# Revit family: Поли-Групп_ЗатворПоворотныйEAZ-EKT_DN100-2000
name_source: partatom
category: Арматура трубопроводов
units: mm (PartAtom-declared; Revit-internal decimal feet)

## family parameters
Всегда вертикально = Да
На основе рабочей плоскости = Нет
Общий = Нет
При загрузке вырезать с полостями = Нет
Размер круглого соединителя = Использовать диаметр
Тип детали = Клапан - Вставляется

## types (38) — shared parameters
ADSK_URL страницы изделия = https://www.polycorr.ru
ADSK_Версия Revit = 2019
ADSK_Единица измерения = шт.
ADSK_Завод-изготовитель = ООО ПК «Поли-Групп»
ADSK_Количество = 1
ADSK_Материал = Высокопрочный чугун GGG-40
ADSK_Материал наименование = Высокопрочный чугун с шаровидным графитом (GGG-40)
r = 10 мм
Изображение типоразмера = <Нет>
Класс герметичности = ГОСТ Р 9544-2015
Материал Диска = Высокопрочный чугун с шаровидным графитом (GGG-40)
Материал уплотнения = EPDM
Материал штурвала = Сталь окрашенная черная
Назначение = Для установки в качестве запорного устройства на трубопроводах
Покрытия = Высококачественное эпоксидное покрытие толщиной 300 мкм
Рабочая среда = Питьевая вода, техническая вода, морская вода
Разработчик = https://3dbim.pro
Срок службы = 50 лет
ТВ = ЗатворПоворотныйEAZ-EKT_DN100-2000_Поли-Групп
Температура рабочей среды = 0 до +70°С
Тип привода = Редуктор
Тип присоединения = Фланцевое

## per-type parameters (varying)
- 100-10: ADSK_Марка=EAZ-BV-1 DN100 PN10; ADSK_Масса=25; ADSK_Масса_Текст=25; ADSK_Наименование=Затвор поворотный EAZ EKT для воды с мягким уплотнением с двойным эксцентриком. фланцевый DN100 PN10; ADSK_Наименование краткое=Затвор поворотный EAZ EKT DN100 PN10; D=220 мм; D2=156 мм; D3=140 мм; D4=110 мм; DN=100 мм; H1=128 мм; H2=165 мм; Kv=1.0 м³/ч; L=190 мм; PN=10.0 бары; W=250 мм; b=19 мм; d1=113 мм; f=3 мм; h1=45 мм; h2=45 мм; l=125 мм; Вал_d=100 мм; Габаритные размеры=190х220х418; Диск_t=5 мм; Крутящий момент=0; Уши_h=220 мм; Уши_h2=156 мм; Фланец_t=41 мм
- 150-10: ADSK_Марка=EAZ-BV-1 DN150 PN10; ADSK_Масса=40; ADSK_Масса_Текст=40; ADSK_Наименование=Затвор поворотный EAZ EKT для воды с мягким уплотнением с двойным эксцентриком. фланцевый DN150 PN10; ADSK_Наименование краткое=Затвор поворотный EAZ EKT DN150 PN10; D=285 мм; D2=211 мм; D3=190 мм; D4=160 мм; DN=150 мм; H1=166 мм; H2=245 мм; Kv=0.6 м³/ч; L=210 мм; PN=10.0 бары; W=250 мм; b=19 мм; d1=113 мм; f=3 мм; h1=45 мм; h2=45 мм; l=125 мм; Вал_d=100 мм; Габаритные размеры=210х285х536; Диск_t=8 мм; Крутящий момент=0; Уши_h=285 мм; Уши_h2=211 мм; Фланец_t=61 мм
- 200-10: ADSK_Марка=EAZ-BV-1 DN200 PN10; ADSK_Масса=52; ADSK_Масса_Текст=52; ADSK_Наименование=Затвор поворотный EAZ EKT для воды с мягким уплотнением с двойным эксцентриком. фланцевый DN200 PN10; ADSK_Наименование краткое=Затвор поворотный EAZ EKT DN200 PN10; D=340 мм; D2=266 мм; D3=240 мм; D4=210 мм; DN=200 мм; H1=196 мм; H2=270 мм; Kv=0.6 м³/ч; L=230 мм; PN=10.0 бары; W=250 мм; b=20 мм; d1=135 мм; f=3 мм; h1=55 мм; h2=45 мм; l=150 мм; Вал_d=120 мм; Габаритные размеры=230х340х591; Диск_t=10 мм; Крутящий момент=60; Уши_h=340 мм; Уши_h2=266 мм; Фланец_t=68 мм
- 250-10: ADSK_Марка=EAZ-BV-1 DN250 PN10; ADSK_Масса=75; ADSK_Масса_Текст=75; ADSK_Наименование=Затвор поворотный EAZ EKT для воды с мягким уплотнением с двойным эксцентриком. фланцевый DN250 PN10; ADSK_Наименование краткое=Затвор поворотный EAZ EKT DN250 PN10; D=395 мм; D2=319 мм; D3=290 мм; D4=260 мм; DN=250 мм; H1=216 мм; H2=305 мм; Kv=0.5 м³/ч; L=250 мм; PN=10.0 бары; W=280 мм; b=22 мм; d1=135 мм; f=3 мм; h1=55 мм; h2=45 мм; l=150 мм; Вал_d=120 мм; Габаритные размеры=250х395х661; Диск_t=13 мм; Крутящий момент=110; Уши_h=395 мм; Уши_h2=319 мм; Фланец_t=76 мм
- 300-10: ADSK_Марка=EAZ-BV-1 DN300 PN10; ADSK_Масса=110; ADSK_Масса_Текст=110; ADSK_Наименование=Затвор поворотный EAZ EKT для воды с мягким уплотнением с двойным эксцентриком. фланцевый DN300 PN10; ADSK_Наименование краткое=Затвор поворотный EAZ EKT DN300 PN10; D=445 мм; D2=370 мм; D3=340 мм; D4=310 мм; DN=300 мм; H1=245 мм; H2=350 мм; Kv=0.4 м³/ч; L=270 мм; PN=10.0 бары; W=320 мм; b=25 мм; d1=158 мм; f=4 мм; h1=70 мм; h2=45 мм; l=175 мм; Вал_d=140 мм; Габаритные размеры=270х445х755; Диск_t=15 мм; Крутящий момент=150; Уши_h=445 мм; Уши_h2=370 мм; Фланец_t=88 мм
- 350-10: ADSK_Марка=EAZ-BV-1 DN350 PN10; ADSK_Масса=140; ADSK_Масса_Текст=140; ADSK_Наименование=Затвор поворотный EAZ EKT для воды с мягким уплотнением с двойным эксцентриком. фланцевый DN350 PN10; ADSK_Наименование краткое=Затвор поворотный EAZ EKT DN350 PN10; D=505 мм; D2=429 мм; D3=390 мм; D4=360 мм; DN=350 мм; H1=285 мм; H2=395 мм; Kv=0.4 м³/ч; L=290 мм; PN=10.0 бары; W=320 мм; b=25 мм; d1=158 мм; f=4 мм; h1=70 мм; h2=45 мм; l=175 мм; Вал_d=140 мм; Габаритные размеры=290х505х840; Диск_t=18 мм; Крутящий момент=240; Уши_h=505 мм; Уши_h2=429 мм; Фланец_t=99 мм
- 400-10: ADSK_Марка=EAZ-BV-1 DN400 PN10; ADSK_Масса=182; ADSK_Масса_Текст=182; ADSK_Наименование=Затвор поворотный EAZ EKT для воды с мягким уплотнением с двойным эксцентриком. фланцевый DN400 PN10; ADSK_Наименование краткое=Затвор поворотный EAZ EKT DN400 PN10; D=565 мм; D2=480 мм; D3=440 мм; D4=410 мм; DN=400 мм; H1=315 мм; H2=485 мм; Kv=0.3 м³/ч; L=310 мм; PN=10.0 бары; W=350 мм; b=25 мм; d1=189 мм; f=4 мм; h1=85 мм; h2=45 мм; l=210 мм; Вал_d=168 мм; Габаритные размеры=310х565х975; Диск_t=20 мм; Крутящий момент=300; Уши_h=565 мм; Уши_h2=480 мм; Фланец_t=121 мм
- 450-10: ADSK_Марка=EAZ-BV-1 DN450 PN10; ADSK_Масса=230; ADSK_Масса_Текст=230; ADSK_Наименование=Затвор поворотный EAZ EKT для воды с мягким уплотнением с двойным эксцентриком. фланцевый DN450 PN10; ADSK_Наименование краткое=Затвор поворотный EAZ EKT DN450 PN10; D=615 мм; D2=530 мм; D3=490 мм; D4=460 мм; DN=450 мм; H1=335 мм; H2=500 мм; Kv=0.5 м³/ч; L=330 мм; PN=10.0 бары; W=350 мм; b=26 мм; d1=189 мм; f=4 мм; h1=85 мм; h2=58 мм; l=210 мм; Вал_d=168 мм; Габаритные размеры=330х615х1010; Диск_t=23 мм; Крутящий момент=360; Уши_h=615 мм; Уши_h2=530 мм; Фланец_t=125 мм
- 500-10: ADSK_Марка=EAZ-BV-1 DN500 PN10; ADSK_Масса=265; ADSK_Масса_Текст=265; ADSK_Наименование=Затвор поворотный EAZ EKT для воды с мягким уплотнением с двойным эксцентриком. фланцевый DN500 PN10; ADSK_Наименование краткое=Затвор поворотный EAZ EKT DN500 PN10; D=670 мм; D2=582 мм; D3=540 мм; D4=510 мм; DN=500 мм; H1=360 мм; H2=545 мм; Kv=0.4 м³/ч; L=350 мм; PN=10.0 бары; W=400 мм; b=27 мм; d1=234 мм; f=4 мм; h1=85 мм; h2=58 мм; l=260 мм; Вал_d=208 мм; Габаритные размеры=350х670х1105; Диск_t=25 мм; Крутящий момент=430; Уши_h=670 мм; Уши_h2=582 мм; Фланец_t=136 мм
- 600-10: ADSK_Марка=EAZ-BV-1 DN600 PN10; ADSK_Масса=396; ADSK_Масса_Текст=396; ADSK_Наименование=Затвор поворотный EAZ EKT для воды с мягким уплотнением с двойным эксцентриком. фланцевый DN600 PN10; ADSK_Наименование краткое=Затвор поворотный EAZ EKT DN600 PN10; D=780 мм; D2=682 мм; D3=640 мм; D4=610 мм; DN=600 мм; H1=425 мм; H2=595 мм; Kv=0.4 м³/ч; L=390 мм; PN=10.0 бары; W=450 мм; b=30 мм; d1=270 мм; f=5 мм; h1=85 мм; h2=58 мм; l=300 мм; Вал_d=240 мм; Габаритные размеры=390х780х1245; Диск_t=30 мм; Крутящий момент=540; Уши_h=780 мм; Уши_h2=682 мм; Фланец_t=149 мм
- 700-10: ADSK_Марка=EAZ-BV-1 DN700 PN10; ADSK_Масса=550; ADSK_Масса_Текст=550; ADSK_Наименование=Затвор поворотный EAZ EKT для воды с мягким уплотнением с двойным эксцентриком. фланцевый DN700 PN10; ADSK_Наименование краткое=Затвор поворотный EAZ EKT DN700 PN10; D=895 мм; D2=794 мм; D3=740 мм; D4=710 мм; DN=700 мм; H1=490 мм; H2=670 мм; Kv=0.4 м³/ч; L=430 мм; PN=10.0 бары; W=450 мм; b=33 мм; d1=270 мм; f=5 мм; h1=85 мм; h2=60 мм; l=300 мм; Вал_d=240 мм; Габаритные размеры=430х895х1385; Диск_t=35 мм; Крутящий момент=690; Уши_h=895 мм; Уши_h2=794 мм; Фланец_t=168 мм
- 800-10: ADSK_Марка=EAZ-BV-1 DN800 PN10; ADSK_Масса=760; ADSK_Масса_Текст=760; ADSK_Наименование=Затвор поворотный EAZ EKT для воды с мягким уплотнением с двойным эксцентриком. фланцевый DN800 PN10; ADSK_Наименование краткое=Затвор поворотный EAZ EKT DN800 PN10; D=1015 мм; D2=901 мм; D3=840 мм; D4=810 мм; DN=800 мм; H1=552 мм; H2=750 мм; Kv=0.3 м³/ч; L=470 мм; PN=10.0 бары; W=500 мм; b=35 мм; d1=270 мм; f=5 мм; h1=85 мм; h2=60 мм; l=300 мм; Вал_d=240 мм; Габаритные размеры=470х1015х1552; Диск_t=40 мм; Крутящий момент=290; Уши_h=1015 мм; Уши_h2=901 мм; Фланец_t=188 мм
- 900-10: ADSK_Марка=EAZ-BV-1 DN900 PN10; ADSK_Масса=870; ADSK_Масса_Текст=870; ADSK_Наименование=Затвор поворотный EAZ EKT для воды с мягким уплотнением с двойным эксцентриком. фланцевый DN900 PN10; ADSK_Наименование краткое=Затвор поворотный EAZ EKT DN900 PN10; D=1115 мм; D2=1001 мм; D3=940 мм; D4=910 мм; DN=900 мм; H1=600 мм; H2=810 мм; Kv=0.3 м³/ч; L=510 мм; PN=10.0 бары; W=500 мм; b=38 мм; d1=315 мм; f=5 мм; h1=100 мм; h2=60 мм; l=350 мм; Вал_d=280 мм; Габаритные размеры=510х1115х1660; Диск_t=45 мм; Крутящий момент=400; Уши_h=1115 мм; Уши_h2=1001 мм; Фланец_t=203 мм
- 1000-10: ADSK_Марка=EAZ-BV-1 DN1000 PN10; ADSK_Масса=1015; ADSK_Масса_Текст=1015; ADSK_Наименование=Затвор поворотный EAZ EKT для воды с мягким уплотнением с двойным эксцентриком. фланцевый DN1000 PN10; ADSK_Наименование краткое=Затвор поворотный EAZ EKT DN1000 PN10; D=1230 мм; D2=1112 мм; D3=1040 мм; D4=1010 мм; DN=1000 мм; H1=665 мм; H2=885 мм; Kv=0.3 м³/ч; L=550 мм; PN=10.0 бары; W=500 мм; b=40 мм; d1=396 мм; f=5 мм; h1=100 мм; h2=60 мм; l=440 мм; Вал_d=352 мм; Габаритные размеры=550х1230х1800; Диск_t=50 мм; Крутящий момент=310; Уши_h=1230 мм; Уши_h2=1112 мм; Фланец_t=221 мм
- 1200-10: ADSK_Марка=EAZ-BV-1 DN1200 PN10; ADSK_Масса=1885; ADSK_Масса_Текст=1885; ADSK_Наименование=Затвор поворотный EAZ EKT для воды с мягким уплотнением с двойным эксцентриком. фланцевый DN1200 PN10; ADSK_Наименование краткое=Затвор поворотный EAZ EKT DN1200 PN10; D=1455 мм; D2=1328 мм; D3=1240 мм; D4=1210 мм; DN=1200 мм; H1=790 мм; H2=1000 мм; Kv=0.6 м³/ч; L=630 мм; PN=10.0 бары; W=600 мм; b=45 мм; d1=396 мм; f=5 мм; h1=100 мм; h2=70 мм; l=440 мм; Вал_d=352 мм; Габаритные размеры=630х1455х2090; Диск_t=60 мм; Крутящий момент=400; Уши_h=1455 мм; Уши_h2=1328 мм; Фланец_t=250 мм
- 1400-10: ADSK_Марка=EAZ-BV-1 DN1400 PN10; ADSK_Масса=3050; ADSK_Масса_Текст=3050; ADSK_Наименование=Затвор поворотный EAZ EKT для воды с мягким уплотнением с двойным эксцентриком. фланцевый DN1400 PN10; ADSK_Наименование краткое=Затвор поворотный EAZ EKT DN1400 PN10; D=1675 мм; D2=1530 мм; D3=1440 мм; D4=1410 мм; DN=1400 мм; H1=916 мм; H2=1180 мм; Kv=0.2 м³/ч; L=710 мм; PN=10.0 бары; W=650 мм; b=46 мм; d1=432 мм; f=5 мм; h1=125 мм; h2=70 мм; l=480 мм; Вал_d=384 мм; Габаритные размеры=710х1675х2421; Диск_t=70 мм; Крутящий момент=390; Уши_h=1675 мм; Уши_h2=1530 мм; Фланец_t=295 мм
- 1600-10: ADSK_Марка=EAZ-BV-1 DN1600 PN10; ADSK_Масса=4080; ADSK_Масса_Текст=4080; ADSK_Наименование=Затвор поворотный EAZ EKT для воды с мягким уплотнением с двойным эксцентриком. фланцевый DN1600 PN10; ADSK_Наименование краткое=Затвор поворотный EAZ EKT DN1600 PN10; D=1915 мм; D2=1750 мм; D3=1640 мм; D4=1610 мм; DN=1600 мм; H1=1045 мм; H2=1350 мм; Kv=0.2 м³/ч; L=790 мм; PN=10.0 бары; W=700 мм; b=49 мм; d1=432 мм; f=5 мм; h1=125 мм; h2=80 мм; l=480 мм; Вал_d=384 мм; Габаритные размеры=790х1915х2745; Диск_t=80 мм; Крутящий момент=360; Уши_h=1915 мм; Уши_h2=1750 мм; Фланец_t=338 мм
- 1800-10: ADSK_Марка=EAZ-BV-1 DN1800 PN10; ADSK_Масса=5895; ADSK_Масса_Текст=5895; ADSK_Наименование=Затвор поворотный EAZ EKT для воды с мягким уплотнением с двойным эксцентриком. фланцевый DN1800 PN10; ADSK_Наименование краткое=Затвор поворотный EAZ EKT DN1800 PN10; D=2115 мм; D2=1950 мм; D3=1840 мм; D4=1810 мм; DN=1800 мм; H1=1160 мм; H2=1450 мм; Kv=1.0 м³/ч; L=870 мм; PN=10.0 бары; W=750 мм; b=52 мм; d1=468 мм; f=5 мм; h1=125 мм; h2=80 мм; l=520 мм; Вал_d=416 мм; Габаритные размеры=870х2115х2985; Диск_t=90 мм; Крутящий момент=0; Уши_h=2115 мм; Уши_h2=1950 мм; Фланец_t=363 мм
- 2000-10: ADSK_Марка=EAZ-BV-1 DN2000 PN10; ADSK_Масса=7000; ADSK_Масса_Текст=7000; ADSK_Наименование=Затвор поворотный EAZ EKT для воды с мягким уплотнением с двойным эксцентриком. фланцевый DN2000 PN10; ADSK_Наименование краткое=Затвор поворотный EAZ EKT DN2000 PN10; D=2325 мм; D2=2150 мм; D3=2040 мм; D4=2010 мм; DN=2000 мм; H1=1315 мм; H2=1680 мм; Kv=1.0 м³/ч; L=950 мм; PN=10.0 бары; W=800 мм; b=55 мм; d1=468 мм; f=5 мм; h1=150 мм; h2=100 мм; l=520 мм; Вал_d=416 мм; Габаритные размеры=950х2325х3395; Диск_t=100 мм; Крутящий момент=0; Уши_h=2325 мм; Уши_h2=2150 мм; Фланец_t=420 мм
- 100-16: ADSK_Марка=EAZ-BV-1 DN100 PN16; ADSK_Масса=25; ADSK_Масса_Текст=25; ADSK_Наименование=Затвор поворотный EAZ EKT для воды с мягким уплотнением с двойным эксцентриком. фланцевый DN100 PN16; ADSK_Наименование краткое=Затвор поворотный EAZ EKT DN100 PN16; D=220 мм; D2=156 мм; D3=140 мм; D4=110 мм; DN=100 мм; H1=128 мм; H2=165 мм; Kv=1.0 м³/ч; L=190 мм; PN=16.0 бары; W=250 мм; b=19 мм; d1=113 мм; f=3 мм; h1=45 мм; h2=45 мм; l=125 мм; Вал_d=100 мм; Габаритные размеры=190х220х418; Диск_t=5 мм; Крутящий момент=0; Уши_h=220 мм; Уши_h2=156 мм; Фланец_t=41 мм
- 150-16: ADSK_Марка=EAZ-BV-1 DN150 PN16; ADSK_Масса=40; ADSK_Масса_Текст=40; ADSK_Наименование=Затвор поворотный EAZ EKT для воды с мягким уплотнением с двойным эксцентриком. фланцевый DN150 PN16; ADSK_Наименование краткое=Затвор поворотный EAZ EKT DN150 PN16; D=285 мм; D2=211 мм; D3=190 мм; D4=160 мм; DN=150 мм; H1=166 мм; H2=245 мм; Kv=0.6 м³/ч; L=210 мм; PN=16.0 бары; W=250 мм; b=19 мм; d1=113 мм; f=3 мм; h1=45 мм; h2=45 мм; l=125 мм; Вал_d=100 мм; Габаритные размеры=210х285х536; Диск_t=8 мм; Крутящий момент=0; Уши_h=285 мм; Уши_h2=211 мм; Фланец_t=61 мм
- 200-16: ADSK_Марка=EAZ-BV-1 DN200 PN16; ADSK_Масса=56; ADSK_Масса_Текст=56; ADSK_Наименование=Затвор поворотный EAZ EKT для воды с мягким уплотнением с двойным эксцентриком. фланцевый DN200 PN16; ADSK_Наименование краткое=Затвор поворотный EAZ EKT DN200 PN16; D=340 мм; D2=266 мм; D3=240 мм; D4=210 мм; DN=200 мм; H1=196 мм; H2=270 мм; Kv=0.6 м³/ч; L=230 мм; PN=16.0 бары; W=250 мм; b=20 мм; d1=135 мм; f=3 мм; h1=55 мм; h2=45 мм; l=150 мм; Вал_d=120 мм; Габаритные размеры=230х340х591; Диск_t=10 мм; Крутящий момент=90; Уши_h=340 мм; Уши_h2=266 мм; Фланец_t=68 мм
- 250-16: ADSK_Марка=EAZ-BV-1 DN250 PN16; ADSK_Масса=85; ADSK_Масса_Текст=85; ADSK_Наименование=Затвор поворотный EAZ EKT для воды с мягким уплотнением с двойным эксцентриком. фланцевый DN250 PN16; ADSK_Наименование краткое=Затвор поворотный EAZ EKT DN250 PN16; D=405 мм; D2=319 мм; D3=290 мм; D4=260 мм; DN=250 мм; H1=216 мм; H2=305 мм; Kv=0.5 м³/ч; L=250 мм; PN=16.0 бары; W=280 мм; b=22 мм; d1=135 мм; f=3 мм; h1=55 мм; h2=45 мм; l=150 мм; Вал_d=120 мм; Габаритные размеры=250х405х661; Диск_t=13 мм; Крутящий момент=150; Уши_h=405 мм; Уши_h2=319 мм; Фланец_t=76 мм
- 300-16: ADSK_Марка=EAZ-BV-1 DN300 PN16; ADSK_Масса=115; ADSK_Масса_Текст=115; ADSK_Наименование=Затвор поворотный EAZ EKT для воды с мягким уплотнением с двойным эксцентриком. фланцевый DN300 PN16; ADSK_Наименование краткое=Затвор поворотный EAZ EKT DN300 PN16; D=460 мм; D2=370 мм; D3=340 мм; D4=310 мм; DN=300 мм; H1=245 мм; H2=350 мм; Kv=0.4 м³/ч; L=270 мм; PN=16.0 бары; W=320 мм; b=25 мм; d1=158 мм; f=4 мм; h1=70 мм; h2=45 мм; l=175 мм; Вал_d=140 мм; Габаритные размеры=270х460х755; Диск_t=15 мм; Крутящий момент=240; Уши_h=460 мм; Уши_h2=370 мм; Фланец_t=88 мм
- 350-16: ADSK_Марка=EAZ-BV-1 DN350 PN16; ADSK_Масса=150; ADSK_Масса_Текст=150; ADSK_Наименование=Затвор поворотный EAZ EKT для воды с мягким уплотнением с двойным эксцентриком. фланцевый DN350 PN16; ADSK_Наименование краткое=Затвор поворотный EAZ EKT DN350 PN16; D=520 мм; D2=429 мм; D3=390 мм; D4=360 мм; DN=350 мм; H1=285 мм; H2=395 мм; Kv=0.4 м³/ч; L=290 мм; PN=16.0 бары; W=320 мм; b=27 мм; d1=158 мм; f=4 мм; h1=70 мм; h2=45 мм; l=175 мм; Вал_d=140 мм; Габаритные размеры=290х520х840; Диск_t=18 мм; Крутящий момент=300; Уши_h=520 мм; Уши_h2=429 мм; Фланец_t=99 мм
- 400-16: ADSK_Марка=EAZ-BV-1 DN400 PN16; ADSK_Масса=205; ADSK_Масса_Текст=205; ADSK_Наименование=Затвор поворотный EAZ EKT для воды с мягким уплотнением с двойным эксцентриком. фланцевый DN400 PN16; ADSK_Наименование краткое=Затвор поворотный EAZ EKT DN400 PN16; D=580 мм; D2=480 мм; D3=440 мм; D4=410 мм; DN=400 мм; H1=315 мм; H2=485 мм; Kv=0.5 м³/ч; L=310 мм; PN=16.0 бары; W=350 мм; b=28 мм; d1=189 мм; f=4 мм; h1=85 мм; h2=45 мм; l=210 мм; Вал_d=168 мм; Габаритные размеры=310х580х975; Диск_t=20 мм; Крутящий момент=370; Уши_h=580 мм; Уши_h2=480 мм; Фланец_t=121 мм
- 450-16: ADSK_Марка=EAZ-BV-1 DN450 PN16; ADSK_Масса=260; ADSK_Масса_Текст=260; ADSK_Наименование=Затвор поворотный EAZ EKT для воды с мягким уплотнением с двойным эксцентриком. фланцевый DN450 PN16; ADSK_Наименование краткое=Затвор поворотный EAZ EKT DN450 PN16; D=640 мм; D2=548 мм; D3=490 мм; D4=460 мм; DN=450 мм; H1=335 мм; H2=500 мм; Kv=0.5 м³/ч; L=330 мм; PN=16.0 бары; W=350 мм; b=30 мм; d1=189 мм; f=4 мм; h1=85 мм; h2=58 мм; l=210 мм; Вал_d=168 мм; Габаритные размеры=330х640х1010; Диск_t=23 мм; Крутящий момент=390; Уши_h=640 мм; Уши_h2=548 мм; Фланец_t=125 мм
- 500-16: ADSK_Марка=EAZ-BV-1 DN500 PN16; ADSK_Масса=320; ADSK_Масса_Текст=320; ADSK_Наименование=Затвор поворотный EAZ EKT для воды с мягким уплотнением с двойным эксцентриком. фланцевый DN500 PN16; ADSK_Наименование краткое=Затвор поворотный EAZ EKT DN500 PN16; D=715 мм; D2=609 мм; D3=540 мм; D4=510 мм; DN=500 мм; H1=360 мм; H2=545 мм; Kv=0.5 м³/ч; L=350 мм; PN=16.0 бары; W=400 мм; b=32 мм; d1=234 мм; f=4 мм; h1=85 мм; h2=58 мм; l=260 мм; Вал_d=208 мм; Габаритные размеры=350х715х1105; Диск_t=25 мм; Крутящий момент=570; Уши_h=715 мм; Уши_h2=609 мм; Фланец_t=136 мм
- 600-16: ADSK_Марка=EAZ-BV-1 DN600 PN16; ADSK_Масса=455; ADSK_Масса_Текст=455; ADSK_Наименование=Затвор поворотный EAZ EKT для воды с мягким уплотнением с двойным эксцентриком. фланцевый DN600 PN16; ADSK_Наименование краткое=Затвор поворотный EAZ EKT DN600 PN16; D=840 мм; D2=720 мм; D3=640 мм; D4=610 мм; DN=600 мм; H1=425 мм; H2=595 мм; Kv=0.5 м³/ч; L=390 мм; PN=16.0 бары; W=450 мм; b=36 мм; d1=270 мм; f=5 мм; h1=85 мм; h2=58 мм; l=300 мм; Вал_d=240 мм; Габаритные размеры=390х840х1245; Диск_t=30 мм; Крутящий момент=790; Уши_h=840 мм; Уши_h2=720 мм; Фланец_t=149 мм
- 700-16: ADSK_Марка=EAZ-BV-1 DN700 PN16; ADSK_Масса=620; ADSK_Масса_Текст=620; ADSK_Наименование=Затвор поворотный EAZ EKT для воды с мягким уплотнением с двойным эксцентриком. фланцевый DN700 PN16; ADSK_Наименование краткое=Затвор поворотный EAZ EKT DN700 PN16; D=910 мм; D2=794 мм; D3=740 мм; D4=710 мм; DN=700 мм; H1=490 мм; H2=670 мм; Kv=0.4 м³/ч; L=430 мм; PN=16.0 бары; W=450 мм; b=40 мм; d1=270 мм; f=5 мм; h1=85 мм; h2=60 мм; l=300 мм; Вал_d=240 мм; Габаритные размеры=430х910х1385; Диск_t=35 мм; Крутящий момент=310; Уши_h=910 мм; Уши_h2=794 мм; Фланец_t=168 мм
- 800-16: ADSK_Марка=EAZ-BV-1 DN800 PN16; ADSK_Масса=791; ADSK_Масса_Текст=791; ADSK_Наименование=Затвор поворотный EAZ EKT для воды с мягким уплотнением с двойным эксцентриком. фланцевый DN800 PN16; ADSK_Наименование краткое=Затвор поворотный EAZ EKT DN800 PN16; D=1025 мм; D2=901 мм; D3=840 мм; D4=810 мм; DN=800 мм; H1=552 мм; H2=750 мм; Kv=0.4 м³/ч; L=470 мм; PN=16.0 бары; W=500 мм; b=43 мм; d1=270 мм; f=5 мм; h1=85 мм; h2=60 мм; l=300 мм; Вал_d=240 мм; Габаритные размеры=470х1025х1552; Диск_t=40 мм; Крутящий момент=460; Уши_h=1025 мм; Уши_h2=901 мм; Фланец_t=188 мм
- 900-16: ADSK_Марка=EAZ-BV-1 DN900 PN16; ADSK_Масса=1001; ADSK_Масса_Текст=1001; ADSK_Наименование=Затвор поворотный EAZ EKT для воды с мягким уплотнением с двойным эксцентриком. фланцевый DN900 PN16; ADSK_Наименование краткое=Затвор поворотный EAZ EKT DN900 PN16; D=1125 мм; D2=1001 мм; D3=940 мм; D4=910 мм; DN=900 мм; H1=600 мм; H2=810 мм; Kv=0.4 м³/ч; L=510 мм; PN=16.0 бары; W=500 мм; b=47 мм; d1=315 мм; f=5 мм; h1=100 мм; h2=60 мм; l=350 мм; Вал_d=280 мм; Габаритные размеры=510х1125х1660; Диск_t=45 мм; Крутящий момент=390; Уши_h=1125 мм; Уши_h2=1001 мм; Фланец_t=203 мм
- 1000-16: ADSK_Марка=EAZ-BV-1 DN1000 PN16; ADSK_Масса=1155; ADSK_Масса_Текст=1155; ADSK_Наименование=Затвор поворотный EAZ EKT для воды с мягким уплотнением с двойным эксцентриком. фланцевый DN1000 PN16; ADSK_Наименование краткое=Затвор поворотный EAZ EKT DN1000 PN16; D=1255 мм; D2=1112 мм; D3=1040 мм; D4=1010 мм; DN=1000 мм; H1=665 мм; H2=885 мм; Kv=0.3 м³/ч; L=550 мм; PN=16.0 бары; W=500 мм; b=50 мм; d1=396 мм; f=5 мм; h1=100 мм; h2=60 мм; l=440 мм; Вал_d=352 мм; Габаритные размеры=550х1255х1800; Диск_t=50 мм; Крутящий момент=450; Уши_h=1255 мм; Уши_h2=1112 мм; Фланец_t=221 мм
- 1200-16: ADSK_Марка=EAZ-BV-1 DN1200 PN16; ADSK_Масса=1947; ADSK_Масса_Текст=1947; ADSK_Наименование=Затвор поворотный EAZ EKT для воды с мягким уплотнением с двойным эксцентриком. фланцевый DN1200 PN16; ADSK_Наименование краткое=Затвор поворотный EAZ EKT DN1200 PN16; D=1485 мм; D2=1328 мм; D3=1240 мм; D4=1210 мм; DN=1200 мм; H1=790 мм; H2=1000 мм; Kv=0.6 м³/ч; L=630 мм; PN=16.0 бары; W=600 мм; b=57 мм; d1=396 мм; f=5 мм; h1=100 мм; h2=70 мм; l=440 мм; Вал_d=352 мм; Габаритные размеры=630х1485х2090; Диск_t=60 мм; Крутящий момент=330; Уши_h=1485 мм; Уши_h2=1328 мм; Фланец_t=250 мм
- 1400-16: ADSK_Марка=EAZ-BV-1 DN1400 PN16; ADSK_Масса=3076; ADSK_Масса_Текст=3076; ADSK_Наименование=Затвор поворотный EAZ EKT для воды с мягким уплотнением с двойным эксцентриком. фланцевый DN1400 PN16; ADSK_Наименование краткое=Затвор поворотный EAZ EKT DN1400 PN16; D=1685 мм; D2=1530 мм; D3=1440 мм; D4=1410 мм; DN=1400 мм; H1=916 мм; H2=1180 мм; Kv=0.3 м³/ч; L=710 мм; PN=16.0 бары; W=650 мм; b=60 мм; d1=432 мм; f=5 мм; h1=125 мм; h2=70 мм; l=480 мм; Вал_d=384 мм; Габаритные размеры=710х1685х2421; Диск_t=70 мм; Крутящий момент=0; Уши_h=1685 мм; Уши_h2=1530 мм; Фланец_t=295 мм
- 1600-16: ADSK_Марка=EAZ-BV-1 DN1600 PN16; ADSK_Масса=4444; ADSK_Масса_Текст=4444; ADSK_Наименование=Затвор поворотный EAZ EKT для воды с мягким уплотнением с двойным эксцентриком. фланцевый DN1600 PN16; ADSK_Наименование краткое=Затвор поворотный EAZ EKT DN1600 PN16; D=1930 мм; D2=1750 мм; D3=1640 мм; D4=1610 мм; DN=1600 мм; H1=1045 мм; H2=1350 мм; Kv=0.3 м³/ч; L=790 мм; PN=16.0 бары; W=700 мм; b=65 мм; d1=432 мм; f=5 мм; h1=125 мм; h2=80 мм; l=480 мм; Вал_d=384 мм; Габаритные размеры=790х1930х2745; Диск_t=80 мм; Крутящий момент=510; Уши_h=1930 мм; Уши_h2=1750 мм; Фланец_t=338 мм
- 1800-16: ADSK_Марка=EAZ-BV-1 DN1800 PN16; ADSK_Масса=6527; ADSK_Масса_Текст=6527; ADSK_Наименование=Затвор поворотный EAZ EKT для воды с мягким уплотнением с двойным эксцентриком. фланцевый DN1800 PN16; ADSK_Наименование краткое=Затвор поворотный EAZ EKT DN1800 PN16; D=2130 мм; D2=1950 мм; D3=1840 мм; D4=1810 мм; DN=1800 мм; H1=1160 мм; H2=1450 мм; Kv=1.0 м³/ч; L=870 мм; PN=16.0 бары; W=750 мм; b=70 мм; d1=468 мм; f=5 мм; h1=125 мм; h2=80 мм; l=520 мм; Вал_d=416 мм; Габаритные размеры=870х2130х2985; Диск_t=90 мм; Крутящий момент=0; Уши_h=2130 мм; Уши_h2=1950 мм; Фланец_t=363 мм
- 2000-16: ADSK_Марка=EAZ-BV-1 DN2000 PN16; ADSK_Масса=8100; ADSK_Масса_Текст=8100; ADSK_Наименование=Затвор поворотный EAZ EKT для воды с мягким уплотнением с двойным эксцентриком. фланцевый DN2000 PN16; ADSK_Наименование краткое=Затвор поворотный EAZ EKT DN2000 PN16; D=2345 мм; D2=2150 мм; D3=2040 мм; D4=2010 мм; DN=2000 мм; H1=1315 мм; H2=1680 мм; Kv=1.0 м³/ч; L=950 мм; PN=16.0 бары; W=800 мм; b=75 мм; d1=468 мм; f=5 мм; h1=150 мм; h2=100 мм; l=520 мм; Вал_d=416 мм; Габаритные размеры=950х2345х3395; Диск_t=100 мм; Крутящий момент=0; Уши_h=2345 мм; Уши_h2=2150 мм; Фланец_t=420 мм
